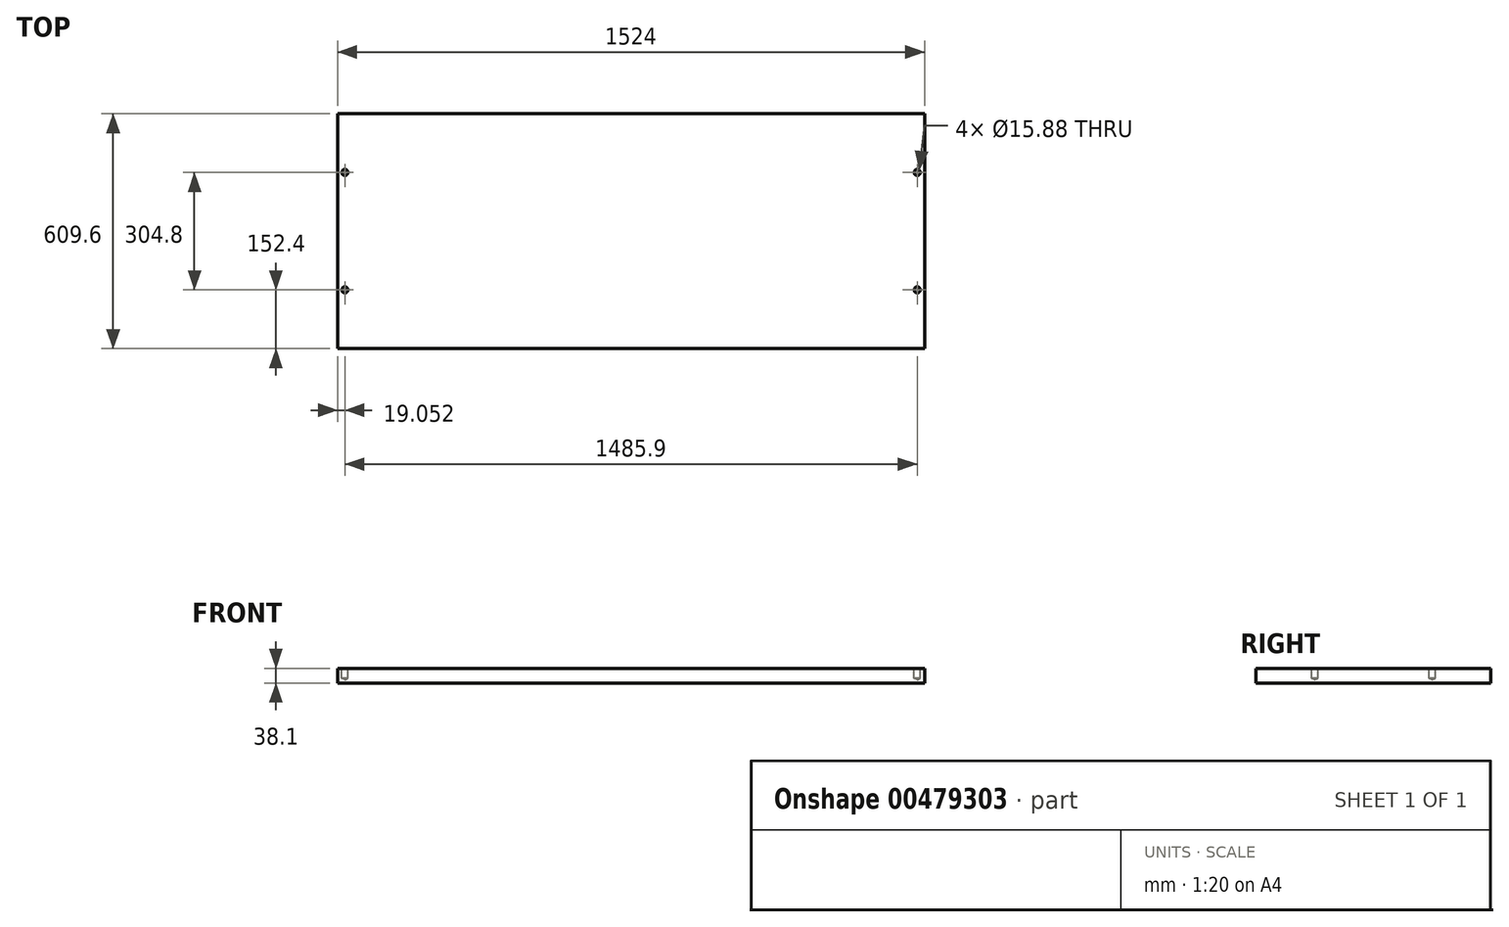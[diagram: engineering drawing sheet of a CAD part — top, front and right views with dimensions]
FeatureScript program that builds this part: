
annotation { "Feature Type Name" : "Feature", "Feature Type Description" : "" }
export const myFeature = defineFeature(function(context is Context, id is Id, definition is map)
    precondition{}
    {
        {
            var Q0;
            Q0=qCreatedBy(makeId("Front.planeOp"),FACE);
            var sketch = newSketch(context, id + "F0", { "sketchPlane" : qUnion([Q0])});
            skLineSegment(sketch, "E0.bottom", {"start": v(59.54, 240.2) * mm, "end": v(1583.54, 240.2) * mm});
            skLineSegment(sketch, "E0.top", {"start": v(59.54, 202.1) * mm, "end": v(1583.54, 202.1) * mm});
            skLineSegment(sketch, "E0.left", {"start": v(59.54, 240.2) * mm, "end": v(59.54, 202.1) * mm});
            skLineSegment(sketch, "E0.right", {"start": v(1583.54, 240.2) * mm, "end": v(1583.54, 202.1) * mm});
            skSolve(sketch);
        }
        {
            var Q0;
            Q0 = qSketchRegion(id + "F0", true);
            extrude(context, id + "F1", {"entities" : qUnion([Q0]), "depth" : -609.6 * mm});
        }
        {
            var Q0;
            Q0=makeQuery(id+"F1.opExtrude","SWEPT_FACE",FACE,{"disambiguationData":[OSD([sQuery(id+"F0.wireOp",EDGE,"E0.bottom")])]});
            var sketch = newSketch(context, id + "F2", { "sketchPlane" : qUnion([Q0])});
            skLineSegment(sketch, "E1", {"start": v(59.54, 322.92) * mm, "end": v(78.6, 322.92) * mm});
            skPoint(sketch, "E2", {"position": v(78.6, 457.2) * mm});
            skPoint(sketch, "E3", {"position": v(78.6, 152.4) * mm});
            skPoint(sketch, "E4", {"position": v(1564.5, 457.2) * mm});
            skPoint(sketch, "E5", {"position": v(1564.5, 152.4) * mm});
            skSolve(sketch);
        }
        {
            var Q0;
            Q0=sQuery(id+"F2.wireOp",VERTEX,"E2");
            var Q1;
            Q1=sQuery(id+"F2.wireOp",VERTEX,"E3");
            var Q2;
            Q2=sQuery(id+"F2.wireOp",VERTEX,"E4");
            var Q3;
            Q3=sQuery(id+"F2.wireOp",VERTEX,"E5");
            var Q4;
            Q4=makeQuery(id+"F1.opExtrude","SWEPT_BODY",BODY,{"disambiguationData":[OSD([sQuery(id+"F0.wireOp",EDGE,"E0.bottom"),sQuery(id+"F0.wireOp",EDGE,"E0.top"),sQuery(id+"F0.wireOp",EDGE,"E0.left"),sQuery(id+"F0.wireOp",EDGE,"E0.right")])]});
            hole(context, id + "F3", {"style" : HoleStyle.SIMPLE, "endStyle" : HoleEndStyle.BLIND, "holeDiameter" : 15.88 * mm, "holeDepth" : 25.4 * mm, "isTappedThrough" : true, "tappedDepth" : 12.7 * mm, "tapClearance" : 3, "locations" : qUnion([Q0, Q1, Q2, Q3]), "scope" : qUnion([Q4])});
        }
    });
